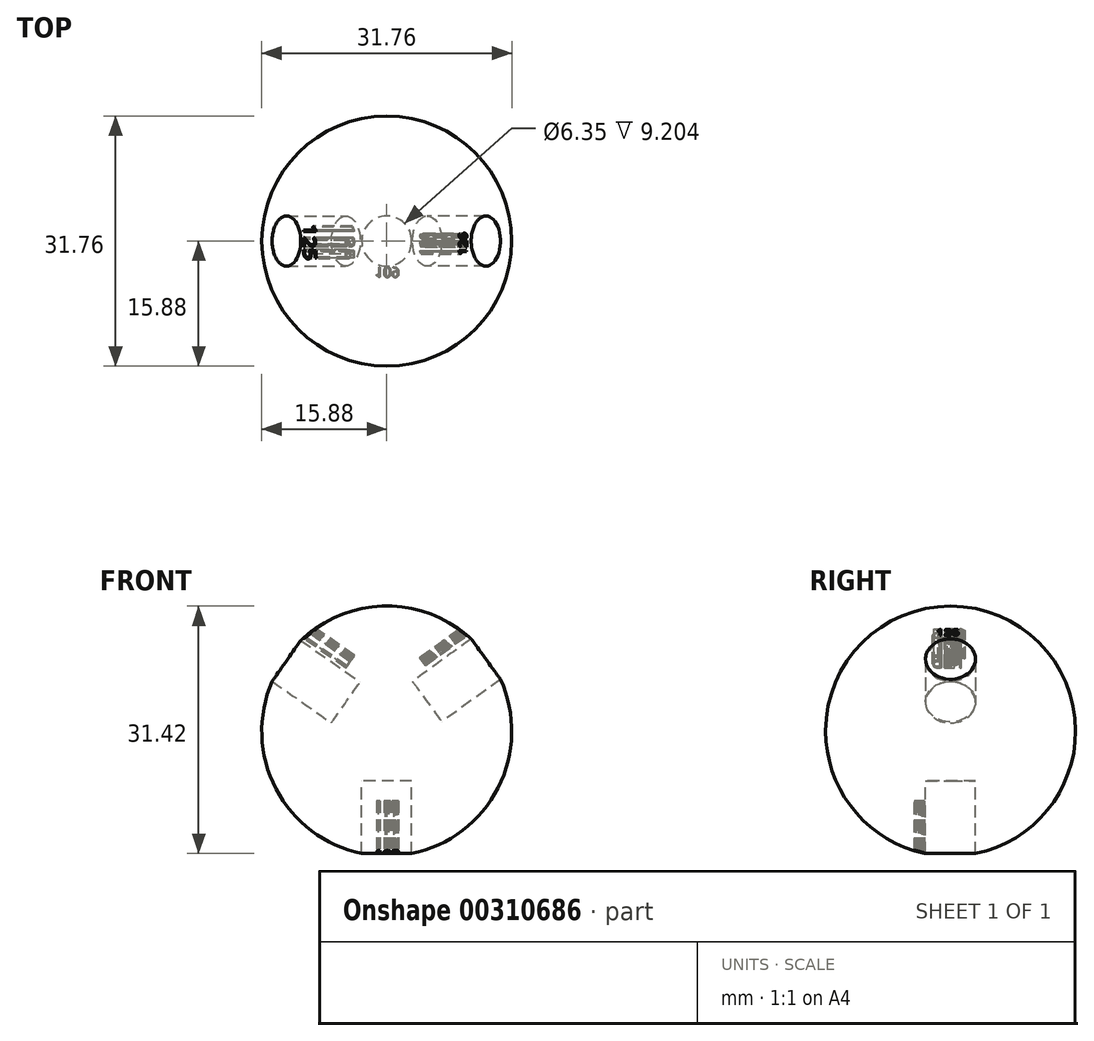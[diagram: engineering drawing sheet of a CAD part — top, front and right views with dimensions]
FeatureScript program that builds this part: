
annotation { "Feature Type Name" : "Feature", "Feature Type Description" : "" }
export const myFeature = defineFeature(function(context is Context, id is Id, definition is map)
    precondition{}
    {
        {
            var Q0;
            Q0=qCreatedBy(makeId("Right.planeOp"),FACE);
            var sketch = newSketch(context, id + "F0", { "sketchPlane" : qUnion([Q0])});
            skArc(sketch, "E0", {"start": v(-15.88, 0) * mm, "mid": v(0, -15.88) * mm, "end": v(15.88, 0) * mm});
            skLineSegment(sketch, "E1", {"start": v(15.88, 0) * mm, "end": v(-15.88, 0) * mm});
            skSolve(sketch);
        }
        {
            var Q0;
            Q0=qCreatedBy(makeId("Front.planeOp"),FACE);
            var sketch = newSketch(context, id + "F1", { "sketchPlane" : qUnion([Q0])});
            skCircle(sketch, "E2", {"center": v(0, 0) * mm, "radius": 15.88 * mm});
            skSolve(sketch);
        }
        {
            var Q0;
            Q0 = qSketchRegion(id + "F0", true);
            var Q1;
            Q1=sQuery(id+"F1.wireOp",EDGE,"E2");
            revolve(context, id + "F2", {"entities" : qUnion([Q0]), "axis" : qUnion([Q1]), "revolveType" : RevolveType.FULL});
        }
        {
            var Q0;
            Q0=qCreatedBy(makeId("Top.planeOp"),FACE);
            cPlane(context, id + "F3", {"entities" : qUnion([Q0]), "cplaneType" : CPlaneType.OFFSET, "offset" : 6.35 * mm, "oppositeDirection" : true, "width" : 152.4 * mm, "height" : 152.4 * mm});
        }
        {
            var Q0;
            Q0=qCreatedBy(id+"F3.planeOp",FACE);
            var sketch = newSketch(context, id + "F4", { "sketchPlane" : qUnion([Q0])});
            skCircle(sketch, "E3", {"center": v(0, 0) * mm, "radius": 3.18 * mm});
            skSolve(sketch);
        }
        {
            var Q0;
            Q0 = qSketchRegion(id + "F4", true);
            extrude(context, id + "F5", {"entities" : qUnion([Q0]), "oppositeDirection" : true, "depth" : 25.4 * mm});
        }
        {
            var Q0;
            Q0=makeQuery(id+"F5.opExtrude","CAP_FACE",FACE,{"disambiguationData":[OSD([sQuery(id+"F4.wireOp",EDGE,"E3")])],"isStart":false});
            cPlane(context, id + "F6", {"entities" : qUnion([Q0]), "cplaneType" : CPlaneType.OFFSET, "offset" : 12.7 * mm, "oppositeDirection" : true, "width" : 152.4 * mm, "height" : 152.4 * mm});
        }
        {
            var Q0;
            Q0=qCreatedBy(id+"F6.planeOp",FACE);
            var sketch = newSketch(context, id + "F7", { "sketchPlane" : qUnion([Q0])});
            skText(sketch, "E4", { "text": "109", "fontName": "OpenSans-Regular.ttf"});
            const initialGuessF7  = {"E4": [-0.00148, 0.00331, 1, 0, 0.0013]};
            skSetInitialGuess(sketch, initialGuessF7);
            skSolve(sketch);
        }
        {
            var Q0;
            Q0 = qSketchRegion(id + "F7", true);
            extrude(context, id + "F8", {"entities" : qUnion([Q0]), "operationType" : NewBodyOperationType.REMOVE, "oppositeDirection" : true, "depth" : 10.16 * mm});
        }
        {
            var Q0;
            Q0=qCreatedBy(makeId("Right.planeOp"),FACE);
            var sketch = newSketch(context, id + "F9", { "sketchPlane" : qUnion([Q0])});
            skLineSegment(sketch, "E5", {"start": v(-53.1, 0) * mm, "end": v(35.95, 0) * mm, "construction": true});
            skSolve(sketch);
        }
        {
            var Q0;
            Q0=makeQuery(id+"F5.opExtrude","SWEPT_BODY",BODY,{"disambiguationData":[OSD([sQuery(id+"F4.wireOp",EDGE,"E3")])]});
            var Q1;
            Q1=sQuery(id+"F9.wireOp",EDGE,"E5");
            transform(context, id + "F10", {"entities" : qUnion([Q0]), "transformType" : TransformType.ROTATION, "transformAxis" : qUnion([Q1]), "angle" : 125 * degree, "makeCopy" : true});
        }
        {
            var Q0;
            Q0=makeQuery(id+"F10.opPattern","COPY",FACE,{"derivedFrom":makeQuery(id+"F5.opExtrude","CAP_FACE",FACE,{"disambiguationData":[OSD([sQuery(id+"F4.wireOp",EDGE,"E3")])],"isStart":false}),"instanceName":"1"});
            cPlane(context, id + "F11", {"entities" : qUnion([Q0]), "cplaneType" : CPlaneType.OFFSET, "offset" : 12.7 * mm, "oppositeDirection" : true, "width" : 152.4 * mm, "height" : 152.4 * mm});
        }
        {
            var Q0;
            Q0=qCreatedBy(id+"F11.planeOp",FACE);
            var sketch = newSketch(context, id + "F12", { "sketchPlane" : qUnion([Q0])});
            skText(sketch, "E6", { "text": "125\n", "fontName": "OpenSans-Regular.ttf"});
            const initialGuessF12  = {"E6": [-0.00212, 0.0036, 1, 0, 0.00191]};
            skSetInitialGuess(sketch, initialGuessF12);
            skSolve(sketch);
        }
        {
            var Q0;
            Q0 = qSketchRegion(id + "F12", true);
            extrude(context, id + "F13", {"entities" : qUnion([Q0]), "operationType" : NewBodyOperationType.REMOVE, "oppositeDirection" : true, "depth" : 10.16 * mm});
        }
        {
            var Q0;
            Q0=qCreatedBy(makeId("Right.planeOp"),FACE);
            var sketch = newSketch(context, id + "F14", { "sketchPlane" : qUnion([Q0])});
            skLineSegment(sketch, "E7", {"start": v(52.73, 0) * mm, "end": v(-57.52, 0) * mm, "construction": true});
            skSolve(sketch);
        }
        {
            var Q0;
            Q0=makeQuery(id+"F5.opExtrude","SWEPT_BODY",BODY,{"disambiguationData":[OSD([sQuery(id+"F4.wireOp",EDGE,"E3")])]});
            var Q1;
            Q1=sQuery(id+"F14.wireOp",EDGE,"E7");
            transform(context, id + "F15", {"entities" : qUnion([Q0]), "transformType" : TransformType.ROTATION, "transformAxis" : qUnion([Q1]), "angle" : 126 * degree, "makeCopy" : true});
        }
        {
            var Q0;
            Q0=makeQuery(id+"F15.opPattern","COPY",FACE,{"derivedFrom":makeQuery(id+"F5.opExtrude","CAP_FACE",FACE,{"disambiguationData":[OSD([sQuery(id+"F4.wireOp",EDGE,"E3")])],"isStart":false}),"instanceName":"1"});
            cPlane(context, id + "F16", {"entities" : qUnion([Q0]), "cplaneType" : CPlaneType.OFFSET, "offset" : 12.7 * mm, "oppositeDirection" : true, "width" : 152.4 * mm, "height" : 152.4 * mm});
        }
        {
            var Q0;
            Q0=qCreatedBy(id+"F16.planeOp",FACE);
            var sketch = newSketch(context, id + "F17", { "sketchPlane" : qUnion([Q0])});
            skText(sketch, "E8", { "text": "126", "fontName": "OpenSans-Regular.ttf"});
            const initialGuessF17  = {"E8": [-0.00178, 0.00386, 1, 0, 0.0012]};
            skSetInitialGuess(sketch, initialGuessF17);
            skSolve(sketch);
        }
        {
            var Q0;
            Q0 = qSketchRegion(id + "F17", true);
            extrude(context, id + "F18", {"entities" : qUnion([Q0]), "operationType" : NewBodyOperationType.REMOVE, "oppositeDirection" : true, "depth" : 10.16 * mm});
        }
        {
            var Q0;
            Q0=makeQuery(id+"F10.opPattern","COPY",BODY,{"derivedFrom":makeQuery(id+"F5.opExtrude","SWEPT_BODY",BODY,{"disambiguationData":[OSD([sQuery(id+"F4.wireOp",EDGE,"E3")])]}),"instanceName":"1"});
            var Q1;
            Q1=makeQuery(id+"F5.opExtrude","SWEPT_BODY",BODY,{"disambiguationData":[OSD([sQuery(id+"F4.wireOp",EDGE,"E3")])]});
            var Q2;
            Q2=makeQuery(id+"F15.opPattern","COPY",BODY,{"derivedFrom":makeQuery(id+"F5.opExtrude","SWEPT_BODY",BODY,{"disambiguationData":[OSD([sQuery(id+"F4.wireOp",EDGE,"E3")])]}),"instanceName":"1"});
            var Q3;
            Q3=makeQuery(id+"F2.opRevolve","SWEPT_BODY",BODY,{"disambiguationData":[OSD([sQuery(id+"F0.wireOp",EDGE,"E0"),sQuery(id+"F0.wireOp",EDGE,"E1")])]});
            booleanBodies(context, id + "F19", {"operationType" : BooleanOperationType.SUBTRACTION, "tools" : qUnion([Q0, Q1, Q2]), "targets" : qUnion([Q3])});
        }
    });
